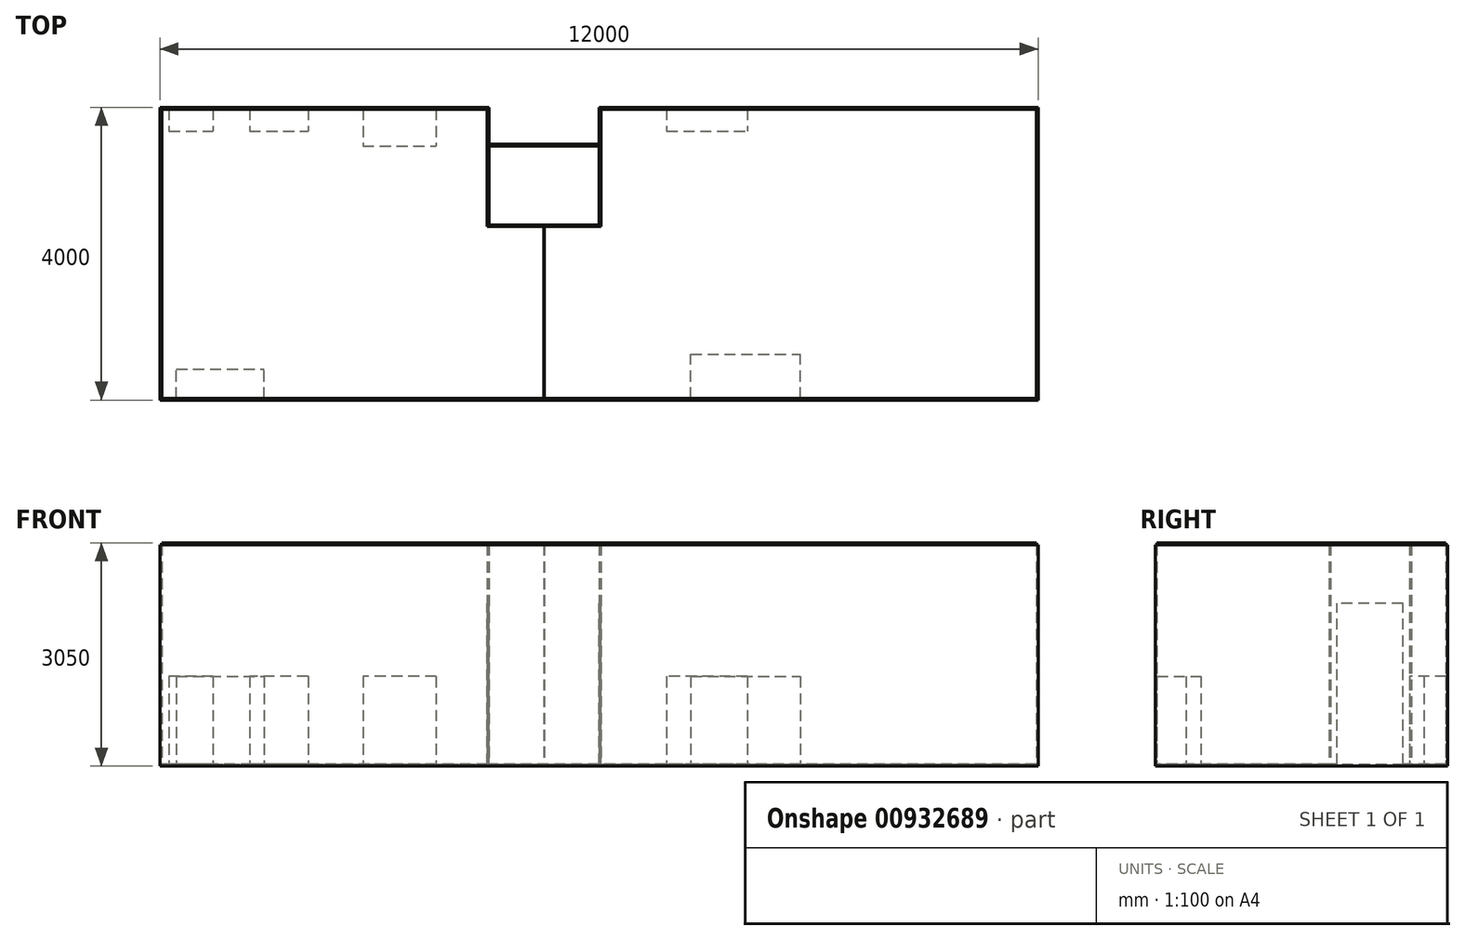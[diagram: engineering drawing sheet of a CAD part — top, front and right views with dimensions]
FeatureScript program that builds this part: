
annotation { "Feature Type Name" : "Feature", "Feature Type Description" : "" }
export const myFeature = defineFeature(function(context is Context, id is Id, definition is map)
    precondition{}
    {
        {
            var Q0;
            Q0=qCreatedBy(makeId("Top.planeOp"),FACE);
            var sketch = newSketch(context, id + "F0", { "sketchPlane" : qUnion([Q0])});
            skLineSegment(sketch, "E0", {"start": v(0, 4000) * mm, "end": v(0, 0) * mm});
            skLineSegment(sketch, "E1", {"start": v(0, 0) * mm, "end": v(12000, 0) * mm});
            skLineSegment(sketch, "E2", {"start": v(12000, 0) * mm, "end": v(12000, 4000) * mm});
            skLineSegment(sketch, "E3", {"start": v(12000, 4000) * mm, "end": v(6000, 4000) * mm});
            skLineSegment(sketch, "E4", {"start": v(6000, 4000) * mm, "end": v(6000, 3500) * mm});
            skLineSegment(sketch, "E5", {"start": v(6000, 3500) * mm, "end": v(4500, 3500) * mm});
            skLineSegment(sketch, "E6", {"start": v(4500, 3500) * mm, "end": v(4500, 4000) * mm});
            skLineSegment(sketch, "E7", {"start": v(4500, 4000) * mm, "end": v(0, 4000) * mm});
            skSolve(sketch);
        }
        {
            var Q0;
            Q0=makeQuery(id+"F0.imprint","IMPRINT",FACE,{"disambiguationData":[TD([[makeQuery(id+"F0.imprint","IMPRINT",EDGE,{"derivedFrom":sQuery(id+"F0.wireOp",EDGE,"E0")}),1.0]])]});
            extrude(context, id + "F1", {"entities" : qUnion([Q0]), "depth" : 25 * mm, "offsetDistance" : 25 * mm});
        }
        {
            var Q0;
            Q0=makeQuery(id+"F1.opExtrude","CAP_FACE",FACE,{"disambiguationData":[OSD([sQuery(id+"F0.wireOp",EDGE,"E0"),sQuery(id+"F0.wireOp",EDGE,"E1"),sQuery(id+"F0.wireOp",EDGE,"E2"),sQuery(id+"F0.wireOp",EDGE,"E3"),sQuery(id+"F0.wireOp",EDGE,"E4"),sQuery(id+"F0.wireOp",EDGE,"E5"),sQuery(id+"F0.wireOp",EDGE,"E6"),sQuery(id+"F0.wireOp",EDGE,"E7")])],"isStart":false});
            var sketch = newSketch(context, id + "F2", { "sketchPlane" : qUnion([Q0])});
            skLineSegment(sketch, "E8", {"start": v(25, 25) * mm, "end": v(11975, 25) * mm});
            skLineSegment(sketch, "E9", {"start": v(11975, 25) * mm, "end": v(11975, 3975) * mm});
            skLineSegment(sketch, "E10", {"start": v(11975, 3975) * mm, "end": v(6025, 3975) * mm});
            skLineSegment(sketch, "E11", {"start": v(6025, 3975) * mm, "end": v(6025, 3475) * mm});
            skLineSegment(sketch, "E12", {"start": v(6025, 3475) * mm, "end": v(4475, 3475) * mm});
            skLineSegment(sketch, "E13", {"start": v(4475, 3475) * mm, "end": v(4475, 3975) * mm});
            skLineSegment(sketch, "E14", {"start": v(4475, 3975) * mm, "end": v(25, 3975) * mm});
            skLineSegment(sketch, "E15", {"start": v(25, 3975) * mm, "end": v(25, 25) * mm});
            skLineSegment(sketch, "E16", {"start": v(4475, 3475) * mm, "end": v(4475, 2375) * mm});
            skLineSegment(sketch, "E17", {"start": v(4475, 2375) * mm, "end": v(6025, 2375) * mm});
            skLineSegment(sketch, "E18", {"start": v(6025, 2375) * mm, "end": v(6025, 3475) * mm});
            skLineSegment(sketch, "E19", {"start": v(4500, 3475) * mm, "end": v(4500, 2395) * mm});
            skLineSegment(sketch, "E20", {"start": v(4500, 2395) * mm, "end": v(6000, 2395) * mm});
            skLineSegment(sketch, "E21", {"start": v(6000, 2395) * mm, "end": v(6000, 3475) * mm});
            skLineSegment(sketch, "E22", {"start": v(5250, 2375) * mm, "end": v(5250, 25) * mm, "construction": true});
            skLineSegment(sketch, "E23", {"start": v(5245, 2375) * mm, "end": v(5245, 25) * mm});
            skLineSegment(sketch, "E24", {"start": v(5255, 2375) * mm, "end": v(5255, 25) * mm});
            skSolve(sketch);
        }
        {
            var Q0;
            Q0=makeQuery(id+"F2.imprint","IMPRINT",FACE,{"disambiguationData":[TD([[makeQuery(id+"F2.imprint","IMPRINT",EDGE,{"derivedFrom":sQuery(id+"F2.wireOp",EDGE,"E8")}),-1.0]])]});
            var Q1;
            {var subQ0=sQuery(id+"F2.wireOp",EDGE,"E16");Q1=makeQuery(id+"F2.imprint","IMPRINT",FACE,{"disambiguationData":[TD([[makeQuery(id+"F2.imprint","IMPRINT",EDGE,{"derivedFrom":subQ0}),1.0]])]});}
            var Q2;
            {var subQ0=sQuery(id+"F2.wireOp",EDGE,"E23");Q2=makeQuery(id+"F2.imprint","IMPRINT",FACE,{"disambiguationData":[TD([[makeQuery(id+"F2.imprint","IMPRINT",EDGE,{"derivedFrom":subQ0}),1.0]])]});}
            extrude(context, id + "F3", {"entities" : qUnion([Q0, Q1, Q2]), "operationType" : NewBodyOperationType.ADD, "depth" : 3000 * mm, "offsetDistance" : 25 * mm});
        }
        {
            var Q0;
            Q0=makeQuery(id+"F3.opExtrude","SWEPT_FACE",FACE,{"disambiguationData":[OSD([sQuery(id+"F2.wireOp",EDGE,"E19")])]});
            var sketch = newSketch(context, id + "F4", { "sketchPlane" : qUnion([Q0])});
            skLineSegment(sketch, "E25.bottom", {"start": v(2485, 25) * mm, "end": v(3385, 25) * mm});
            skLineSegment(sketch, "E25.top", {"start": v(2485, 2225) * mm, "end": v(3385, 2225) * mm});
            skLineSegment(sketch, "E25.left", {"start": v(2485, 25) * mm, "end": v(2485, 2225) * mm});
            skLineSegment(sketch, "E25.right", {"start": v(3385, 25) * mm, "end": v(3385, 2225) * mm});
            skSolve(sketch);
        }
        {
            var Q0;
            Q0=makeQuery(id+"F4.imprint","IMPRINT",FACE,{"disambiguationData":[TD([[makeQuery(id+"F4.imprint","IMPRINT",EDGE,{"derivedFrom":sQuery(id+"F4.wireOp",EDGE,"E25.bottom")}),-1.0]])]});
            var Q1;
            Q1=makeQuery(id+"F1.opExtrude","SWEPT_BODY",BODY,{"disambiguationData":[OSD([sQuery(id+"F0.wireOp",EDGE,"E0"),sQuery(id+"F0.wireOp",EDGE,"E1"),sQuery(id+"F0.wireOp",EDGE,"E2"),sQuery(id+"F0.wireOp",EDGE,"E3"),sQuery(id+"F0.wireOp",EDGE,"E4"),sQuery(id+"F0.wireOp",EDGE,"E5"),sQuery(id+"F0.wireOp",EDGE,"E6"),sQuery(id+"F0.wireOp",EDGE,"E7")])]});
            extrude(context, id + "F5", {"entities" : qUnion([Q0]), "operationType" : NewBodyOperationType.REMOVE, "endBound" : BoundingType.UP_TO_BODY, "oppositeDirection" : true, "depth" : 25 * mm, "endBoundEntityBody" : qUnion([Q1]), "offsetDistance" : 25 * mm});
        }
        {
            var Q0;
            Q0=makeQuery(id+"F3.opExtrude","SWEPT_FACE",FACE,{"disambiguationData":[OSD([sQuery(id+"F2.wireOp",EDGE,"E21")])]});
            var sketch = newSketch(context, id + "F6", { "sketchPlane" : qUnion([Q0])});
            skLineSegment(sketch, "E26.bottom", {"start": v(-3385, 25) * mm, "end": v(-2485, 25) * mm});
            skLineSegment(sketch, "E26.top", {"start": v(-3385, 2225) * mm, "end": v(-2485, 2225) * mm});
            skLineSegment(sketch, "E26.left", {"start": v(-3385, 25) * mm, "end": v(-3385, 2225) * mm});
            skLineSegment(sketch, "E26.right", {"start": v(-2485, 25) * mm, "end": v(-2485, 2225) * mm});
            skSolve(sketch);
        }
        {
            var Q0;
            Q0=makeQuery(id+"F6.imprint","IMPRINT",FACE,{"disambiguationData":[TD([[makeQuery(id+"F6.imprint","IMPRINT",EDGE,{"derivedFrom":sQuery(id+"F6.wireOp",EDGE,"E26.bottom")}),-1.0]])]});
            var Q1;
            Q1=makeQuery(id+"F1.opExtrude","SWEPT_BODY",BODY,{"disambiguationData":[OSD([sQuery(id+"F0.wireOp",EDGE,"E0"),sQuery(id+"F0.wireOp",EDGE,"E1"),sQuery(id+"F0.wireOp",EDGE,"E2"),sQuery(id+"F0.wireOp",EDGE,"E3"),sQuery(id+"F0.wireOp",EDGE,"E4"),sQuery(id+"F0.wireOp",EDGE,"E5"),sQuery(id+"F0.wireOp",EDGE,"E6"),sQuery(id+"F0.wireOp",EDGE,"E7")])]});
            extrude(context, id + "F7", {"entities" : qUnion([Q0]), "operationType" : NewBodyOperationType.REMOVE, "endBound" : BoundingType.UP_TO_BODY, "oppositeDirection" : true, "depth" : 25 * mm, "endBoundEntityBody" : qUnion([Q1]), "offsetDistance" : 25 * mm});
        }
        {
            var Q0;
            {var subQ0=makeQuery(id+"F1.opExtrude","CAP_FACE",FACE,{"disambiguationData":[OSD([sQuery(id+"F0.wireOp",EDGE,"E0"),sQuery(id+"F0.wireOp",EDGE,"E1"),sQuery(id+"F0.wireOp",EDGE,"E2"),sQuery(id+"F0.wireOp",EDGE,"E3"),sQuery(id+"F0.wireOp",EDGE,"E4"),sQuery(id+"F0.wireOp",EDGE,"E5"),sQuery(id+"F0.wireOp",EDGE,"E6"),sQuery(id+"F0.wireOp",EDGE,"E7")])],"isStart":false});var subQ8=sQuery(id+"F2.wireOp",EDGE,"E9");Q0=makeQuery(id+"F7.boolean.opBoolean","MERGE",FACE,{"derivedFrom":[makeQuery(id+"F3.boolean.opBoolean","SPLIT",FACE,{"disambiguationData":[TD([makeQuery(id+"F3.opExtrude","SWEPT_FACE",FACE,{"disambiguationData":[OSD([subQ8])]})])],"derivedFrom":subQ0}),makeQuery(id+"F5.boolean.opBoolean","MERGE",FACE,{"derivedFrom":[makeQuery(id+"F3.boolean.opBoolean","SPLIT",FACE,{"disambiguationData":[TD([makeQuery(id+"F3.opExtrude","SWEPT_FACE",FACE,{"disambiguationData":[OSD([sQuery(id+"F2.wireOp",EDGE,"E14")])]})])],"derivedFrom":subQ0}),makeQuery(id+"F3.boolean.opBoolean","SPLIT",FACE,{"disambiguationData":[TD([makeQuery(id+"F3.opExtrude","SWEPT_FACE",FACE,{"disambiguationData":[OSD([sQuery(id+"F2.wireOp",EDGE,"E12")])]})])],"derivedFrom":subQ0})],"fromTools":[makeQuery(id+"F5.opExtrude","SWEPT_FACE",FACE,{"disambiguationData":[OSD([sQuery(id+"F4.wireOp",EDGE,"E25.bottom")])]})]})],"fromTools":[makeQuery(id+"F7.opExtrude","SWEPT_FACE",FACE,{"disambiguationData":[OSD([sQuery(id+"F6.wireOp",EDGE,"E26.bottom")])]})]});}
            var sketch = newSketch(context, id + "F8", { "sketchPlane" : qUnion([Q0])});
            skLineSegment(sketch, "E27.bottom", {"start": v(125, 3975) * mm, "end": v(725, 3975) * mm});
            skLineSegment(sketch, "E27.top", {"start": v(125, 3675) * mm, "end": v(725, 3675) * mm});
            skLineSegment(sketch, "E27.left", {"start": v(125, 3975) * mm, "end": v(125, 3675) * mm});
            skLineSegment(sketch, "E27.right", {"start": v(725, 3975) * mm, "end": v(725, 3675) * mm});
            skLineSegment(sketch, "E28.bottom", {"start": v(1225, 3975) * mm, "end": v(2025, 3975) * mm});
            skLineSegment(sketch, "E28.top", {"start": v(1225, 3675) * mm, "end": v(2025, 3675) * mm});
            skLineSegment(sketch, "E28.left", {"start": v(1225, 3975) * mm, "end": v(1225, 3675) * mm});
            skLineSegment(sketch, "E28.right", {"start": v(2025, 3975) * mm, "end": v(2025, 3675) * mm});
            skLineSegment(sketch, "E29.bottom", {"start": v(2775, 3975) * mm, "end": v(3775, 3975) * mm});
            skLineSegment(sketch, "E29.top", {"start": v(2775, 3475) * mm, "end": v(3775, 3475) * mm});
            skLineSegment(sketch, "E29.left", {"start": v(2775, 3975) * mm, "end": v(2775, 3475) * mm});
            skLineSegment(sketch, "E29.right", {"start": v(3775, 3975) * mm, "end": v(3775, 3475) * mm});
            skLineSegment(sketch, "E30.bottom", {"start": v(225, 25) * mm, "end": v(1425, 25) * mm});
            skLineSegment(sketch, "E30.top", {"start": v(225, 425) * mm, "end": v(1425, 425) * mm});
            skLineSegment(sketch, "E30.left", {"start": v(225, 25) * mm, "end": v(225, 425) * mm});
            skLineSegment(sketch, "E30.right", {"start": v(1425, 25) * mm, "end": v(1425, 425) * mm});
            skLineSegment(sketch, "E31.bottom", {"start": v(6925, 3975) * mm, "end": v(8025, 3975) * mm});
            skLineSegment(sketch, "E31.top", {"start": v(6925, 3675) * mm, "end": v(8025, 3675) * mm});
            skLineSegment(sketch, "E31.left", {"start": v(6925, 3975) * mm, "end": v(6925, 3675) * mm});
            skLineSegment(sketch, "E31.right", {"start": v(8025, 3975) * mm, "end": v(8025, 3675) * mm});
            skLineSegment(sketch, "E32.bottom", {"start": v(7255, 25) * mm, "end": v(8755, 25) * mm});
            skLineSegment(sketch, "E32.top", {"start": v(7255, 625) * mm, "end": v(8755, 625) * mm});
            skLineSegment(sketch, "E32.left", {"start": v(7255, 25) * mm, "end": v(7255, 625) * mm});
            skLineSegment(sketch, "E32.right", {"start": v(8755, 25) * mm, "end": v(8755, 625) * mm});
            skSolve(sketch);
        }
        {
            var Q0;
            Q0=makeQuery(id+"F8.imprint","IMPRINT",FACE,{"disambiguationData":[TD([[makeQuery(id+"F8.imprint","IMPRINT",EDGE,{"derivedFrom":sQuery(id+"F8.wireOp",EDGE,"E27.bottom")}),1.0]])]});
            var Q1;
            Q1=makeQuery(id+"F8.imprint","IMPRINT",FACE,{"disambiguationData":[TD([[makeQuery(id+"F8.imprint","IMPRINT",EDGE,{"derivedFrom":sQuery(id+"F8.wireOp",EDGE,"E28.bottom")}),1.0]])]});
            var Q2;
            Q2=makeQuery(id+"F8.imprint","IMPRINT",FACE,{"disambiguationData":[TD([[makeQuery(id+"F8.imprint","IMPRINT",EDGE,{"derivedFrom":sQuery(id+"F8.wireOp",EDGE,"E29.bottom")}),1.0]])]});
            var Q3;
            Q3=makeQuery(id+"F8.imprint","IMPRINT",FACE,{"disambiguationData":[TD([[makeQuery(id+"F8.imprint","IMPRINT",EDGE,{"derivedFrom":sQuery(id+"F8.wireOp",EDGE,"E30.bottom")}),1.0]])]});
            var Q4;
            Q4=makeQuery(id+"F8.imprint","IMPRINT",FACE,{"disambiguationData":[TD([[makeQuery(id+"F8.imprint","IMPRINT",EDGE,{"derivedFrom":sQuery(id+"F8.wireOp",EDGE,"E32.bottom")}),1.0]])]});
            var Q5;
            Q5=makeQuery(id+"F8.imprint","IMPRINT",FACE,{"disambiguationData":[TD([[makeQuery(id+"F8.imprint","IMPRINT",EDGE,{"derivedFrom":sQuery(id+"F8.wireOp",EDGE,"E31.bottom")}),1.0]])]});
            extrude(context, id + "F9", {"entities" : qUnion([Q0, Q1, Q2, Q3, Q4, Q5]), "depth" : 1200 * mm, "offsetDistance" : 25 * mm});
        }
        {
            var Q0;
            Q0=makeQuery(id+"F3.opExtrude","CAP_FACE",FACE,{"disambiguationData":[OSD([sQuery(id+"F0.wireOp",EDGE,"E0"),sQuery(id+"F0.wireOp",EDGE,"E1"),sQuery(id+"F0.wireOp",EDGE,"E2"),sQuery(id+"F0.wireOp",EDGE,"E3"),sQuery(id+"F0.wireOp",EDGE,"E4"),sQuery(id+"F0.wireOp",EDGE,"E5"),sQuery(id+"F0.wireOp",EDGE,"E6"),sQuery(id+"F0.wireOp",EDGE,"E7"),sQuery(id+"F2.wireOp",EDGE,"E8"),sQuery(id+"F2.wireOp",EDGE,"E9"),sQuery(id+"F2.wireOp",EDGE,"E10"),sQuery(id+"F2.wireOp",EDGE,"E11"),sQuery(id+"F2.wireOp",EDGE,"E12"),sQuery(id+"F2.wireOp",EDGE,"E13"),sQuery(id+"F2.wireOp",EDGE,"E14"),sQuery(id+"F2.wireOp",EDGE,"E15"),sQuery(id+"F2.wireOp",EDGE,"E16"),sQuery(id+"F2.wireOp",EDGE,"E17"),sQuery(id+"F2.wireOp",EDGE,"E18"),sQuery(id+"F2.wireOp",EDGE,"E19"),sQuery(id+"F2.wireOp",EDGE,"E20"),sQuery(id+"F2.wireOp",EDGE,"E21"),sQuery(id+"F2.wireOp",EDGE,"E23"),sQuery(id+"F2.wireOp",EDGE,"E24")])],"isStart":false});
            var sketch = newSketch(context, id + "F10", { "sketchPlane" : qUnion([Q0])});
            skLineSegment(sketch, "E33.bottom", {"start": v(0, 4000) * mm, "end": v(12000, 4000) * mm});
            skLineSegment(sketch, "E33.top", {"start": v(0, 0) * mm, "end": v(12000, 0) * mm});
            skLineSegment(sketch, "E33.left", {"start": v(0, 4000) * mm, "end": v(0, 0) * mm});
            skLineSegment(sketch, "E33.right", {"start": v(12000, 4000) * mm, "end": v(12000, 0) * mm});
            skSolve(sketch);
        }
        {
            var Q0;
            {var subQ2=sQuery(id+"F2.wireOp",EDGE,"E9");Q0=makeQuery(id+"F10.imprint","IMPRINT",FACE,{"disambiguationData":[TD([[makeQuery(id+"F10.imprint","IMPRINT",EDGE,{"derivedFrom":makeQuery(id+"F3.opExtrude","CAP_EDGE",EDGE,{"disambiguationData":[OSD([subQ2])],"isStart":false})}),1.0]])]});}
            var Q1;
            Q1=makeQuery(id+"F10.imprint","IMPRINT",FACE,{"disambiguationData":[TD([[makeQuery(id+"F10.imprint","IMPRINT",EDGE,{"derivedFrom":makeQuery(id+"F3.opExtrude","CAP_EDGE",EDGE,{"disambiguationData":[OSD([sQuery(id+"F2.wireOp",EDGE,"E14")])],"isStart":false})}),1.0]])]});
            var Q2;
            Q2=makeQuery(id+"F10.imprint","IMPRINT",FACE,{"disambiguationData":[TD([[makeQuery(id+"F10.imprint","IMPRINT",EDGE,{"derivedFrom":makeQuery(id+"F3.opExtrude","CAP_EDGE",EDGE,{"disambiguationData":[OSD([sQuery(id+"F2.wireOp",EDGE,"E12")])],"isStart":false})}),1.0]])]});
            extrude(context, id + "F11", {"entities" : qUnion([Q0, Q1, Q2]), "depth" : 25 * mm, "offsetDistance" : 25 * mm});
        }
    });
